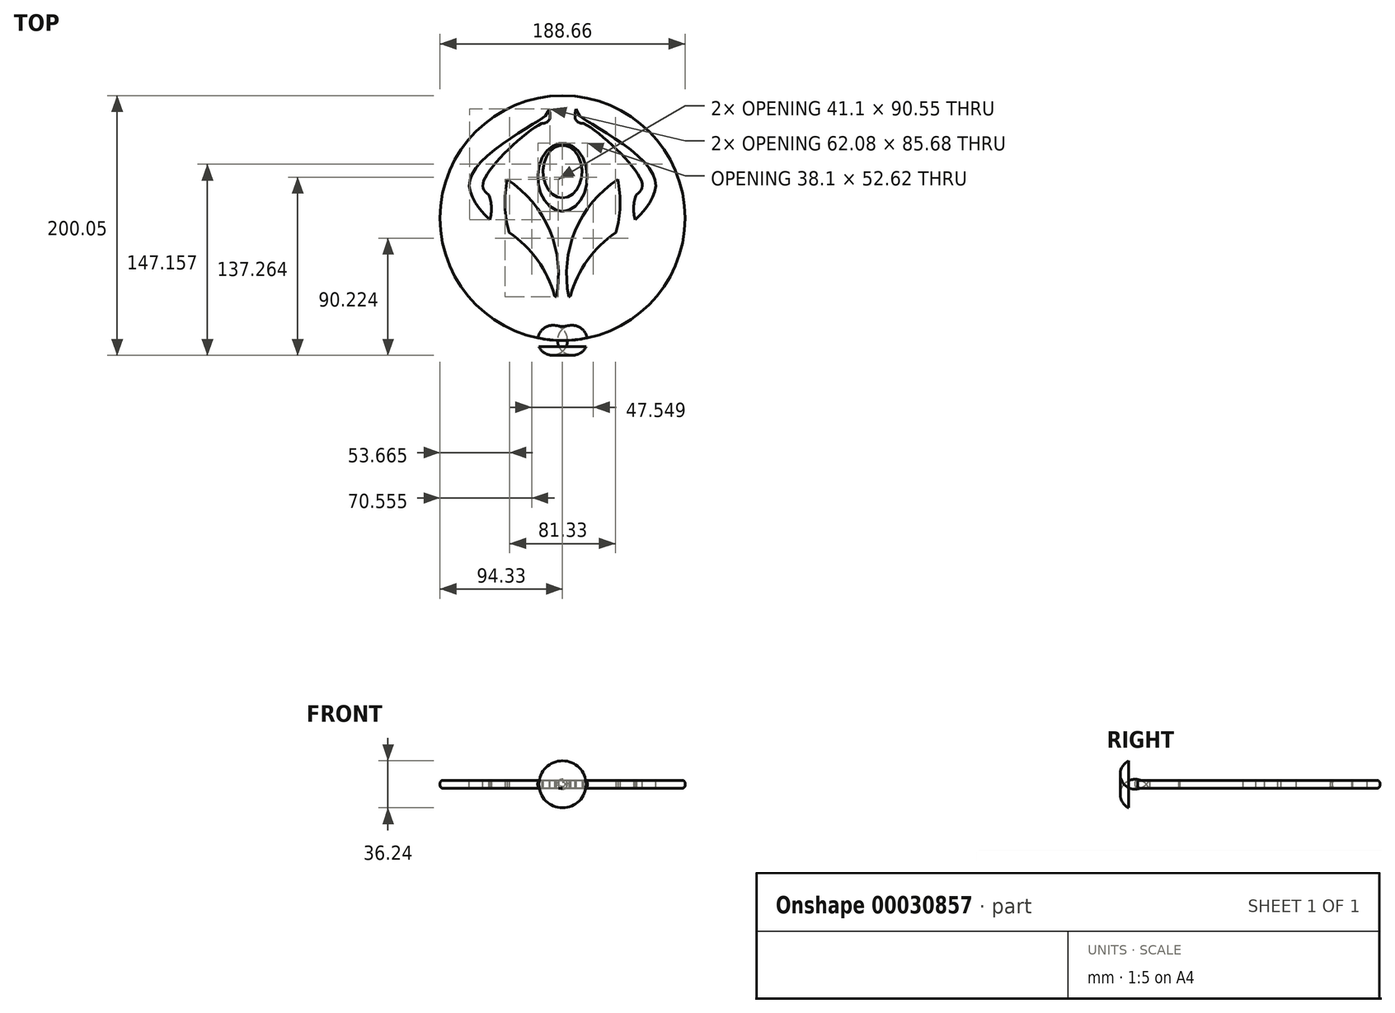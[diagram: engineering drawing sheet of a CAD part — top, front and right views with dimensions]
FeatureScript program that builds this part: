
annotation { "Feature Type Name" : "Feature", "Feature Type Description" : "" }
export const myFeature = defineFeature(function(context is Context, id is Id, definition is map)
    precondition{}
    {
        {
            var Q0;
            Q0=qCreatedBy(makeId("Top.planeOp"),FACE);
            var sketch = newSketch(context, id + "F0", { "sketchPlane" : qUnion([Q0])});
            skLineSegment(sketch, "E0", {"start": v(-75.5, -12.71) * mm, "end": v(-9.56, -74.3) * mm, "construction": true});
            skLineSegment(sketch, "E1", {"start": v(-4.86, -71.61) * mm, "end": v(-42.6, 18.94) * mm, "construction": true});
            skArc(sketch, "E2", {"start": v(-75.5, -12.71) * mm, "mid": v(-51.74, -53.37) * mm, "end": v(-9.56, -74.3) * mm});
            skArc(sketch, "E3", {"start": v(-4.86, -71.61) * mm, "mid": v(-9.83, -20.55) * mm, "end": v(-42.6, 18.94) * mm});
            skArc(sketch, "E4.MirrorCS", {"start": v(-75.5, -12.71) * mm, "mid": v(-33.32, -33.65) * mm, "end": v(-9.56, -74.3) * mm});
            skArc(sketch, "E5.0", {"start": v(-41.12, -22.06) * mm, "mid": v(-19.25, -43.28) * mm, "end": v(-6.12, -70.78) * mm});
            skArc(sketch, "E6.MirrorCS", {"start": v(-4.86, -71.61) * mm, "mid": v(-5.5, -71.2) * mm, "end": v(-6.12, -70.78) * mm});
            skArc(sketch, "E7.trimOffspring", {"start": v(-41.12, -22.06) * mm, "mid": v(-44.3, -1.65) * mm, "end": v(-42.6, 18.94) * mm});
            skArc(sketch, "E8.MirrorCS", {"start": v(75.5, -12.71) * mm, "mid": v(51.74, -53.37) * mm, "end": v(9.56, -74.3) * mm});
            skArc(sketch, "E9.MirrorCS", {"start": v(75.5, -12.71) * mm, "mid": v(33.32, -33.65) * mm, "end": v(9.56, -74.3) * mm});
            skArc(sketch, "E10.MirrorCS", {"start": v(41.12, -22.06) * mm, "mid": v(44.3, -1.65) * mm, "end": v(42.6, 18.94) * mm});
            skArc(sketch, "E11.MirrorCS", {"start": v(41.12, -22.06) * mm, "mid": v(19.25, -43.28) * mm, "end": v(6.12, -70.78) * mm});
            skArc(sketch, "E12.MirrorCS", {"start": v(4.86, -71.61) * mm, "mid": v(9.83, -20.55) * mm, "end": v(42.6, 18.94) * mm});
            skArc(sketch, "E13.MirrorCS", {"start": v(4.86, -71.61) * mm, "mid": v(5.5, -71.2) * mm, "end": v(6.12, -70.78) * mm});
            skFitSpline(sketch, "E14", {"points": [v(-10.08, 72.14) * mm, v(-14.37, 65.7) * mm, v(-68.94, 22.84) * mm, v(-55.76, -13.54) * mm], "startDerivative": vector(-33.58, -68.78) * mm, "endDerivative": vector(100.58, -102.34) * mm});
            skArc(sketch, "E15", {"start": v(-55.76, -13.54) * mm, "mid": v(-54.5, -3.73) * mm, "end": v(-56.62, 5.94) * mm});
            skFitSpline(sketch, "E16", {"points": [v(-56.62, 5.94) * mm, v(-60.66, 15.94) * mm, v(-15.88, 60.9) * mm], "startDerivative": vector(-32.39, 22.42) * mm, "endDerivative": vector(56.1, 28.88) * mm});
            skFitSpline(sketch, "E17", {"points": [v(-10.08, 72.14) * mm, v(-10.08, 63.33) * mm, v(-15.88, 60.9) * mm], "startDerivative": vector(3.32, -19.88) * mm, "endDerivative": vector(-13.95, 1.21) * mm});
            skFitSpline(sketch, "E18.MirrorCS", {"points": [v(10.57, 72.14) * mm, v(10.57, 63.33) * mm, v(16.38, 60.9) * mm], "startDerivative": vector(-3.32, -19.88) * mm, "endDerivative": vector(13.95, 1.21) * mm});
            skFitSpline(sketch, "E19.MirrorCS", {"points": [v(10.57, 72.14) * mm, v(14.86, 65.7) * mm, v(69.43, 22.84) * mm, v(56.26, -13.54) * mm], "startDerivative": vector(33.58, -68.78) * mm, "endDerivative": vector(-100.58, -102.34) * mm});
            skFitSpline(sketch, "E20.MirrorCS", {"points": [v(57.12, 5.94) * mm, v(61.15, 15.94) * mm, v(16.38, 60.9) * mm], "startDerivative": vector(32.39, 22.42) * mm, "endDerivative": vector(-56.1, 28.88) * mm});
            skArc(sketch, "E21.MirrorCS", {"start": v(56.26, -13.54) * mm, "mid": v(55, -3.73) * mm, "end": v(57.12, 5.94) * mm});
            skEllipse(sketch, "E22", {"center": v(0, 20.14) * mm, "majorRadius": 26.3 * mm, "minorRadius": 19.05 * mm, "majorAxis": v(0, -1)});
            skEllipse(sketch, "E23", {"center": v(0, 24.44) * mm, "majorRadius": 20.32 * mm, "minorRadius": 15 * mm, "majorAxis": v(0, -1)});
            skSolve(sketch);
        }
        {
            var Q0;
            Q0=qCreatedBy(makeId("Top.planeOp"),FACE);
            var sketch = newSketch(context, id + "F1", { "sketchPlane" : qUnion([Q0])});
            skEllipse(sketch, "E24", {"center": v(0, 20.7) * mm, "majorRadius": 26.3 * mm, "minorRadius": 19.05 * mm, "majorAxis": v(0, -1)});
            skEllipse(sketch, "E25", {"center": v(0, 25) * mm, "majorRadius": 20.32 * mm, "minorRadius": 15 * mm, "majorAxis": v(0, -1)});
            skSolve(sketch);
        }
        {
            var Q0;
            Q0=qCreatedBy(makeId("Top.planeOp"),FACE);
            var sketch = newSketch(context, id + "F2", { "sketchPlane" : qUnion([Q0])});
            skFitSpline(sketch, "E26", {"points": [v(-10.32, 73.44) * mm, v(-14.62, 66.99) * mm, v(-69.19, 24.14) * mm, v(-56, -12.24) * mm], "startDerivative": vector(-33.58, -68.78) * mm, "endDerivative": vector(100.58, -102.34) * mm});
            skArc(sketch, "E27", {"start": v(-56, -12.24) * mm, "mid": v(-54.75, -2.43) * mm, "end": v(-56.87, 7.24) * mm});
            skFitSpline(sketch, "E28", {"points": [v(-56.87, 7.24) * mm, v(-60.9, 17.24) * mm, v(-16.13, 62.2) * mm], "startDerivative": vector(-32.39, 22.42) * mm, "endDerivative": vector(56.1, 28.88) * mm});
            skFitSpline(sketch, "E29", {"points": [v(-10.32, 73.44) * mm, v(-10.32, 64.63) * mm, v(-16.13, 62.2) * mm], "startDerivative": vector(3.32, -19.88) * mm, "endDerivative": vector(-13.95, 1.21) * mm});
            skFitSpline(sketch, "E30.MirrorCS", {"points": [v(10.32, 73.44) * mm, v(10.32, 64.63) * mm, v(16.13, 62.2) * mm], "startDerivative": vector(-3.32, -19.88) * mm, "endDerivative": vector(13.95, 1.21) * mm});
            skFitSpline(sketch, "E31.MirrorCS", {"points": [v(10.32, 73.44) * mm, v(14.62, 66.99) * mm, v(69.19, 24.14) * mm, v(56, -12.24) * mm], "startDerivative": vector(33.58, -68.78) * mm, "endDerivative": vector(-100.58, -102.34) * mm});
            skFitSpline(sketch, "E32.MirrorCS", {"points": [v(56.87, 7.24) * mm, v(60.9, 17.24) * mm, v(16.13, 62.2) * mm], "startDerivative": vector(32.39, 22.42) * mm, "endDerivative": vector(-56.1, 28.88) * mm});
            skArc(sketch, "E33.MirrorCS", {"start": v(56, -12.24) * mm, "mid": v(54.75, -2.43) * mm, "end": v(56.87, 7.24) * mm});
            skSolve(sketch);
        }
        {
            var Q0;
            Q0=qCreatedBy(makeId("Top.planeOp"),FACE);
            var sketch = newSketch(context, id + "F3", { "sketchPlane" : qUnion([Q0])});
            skCircle(sketch, "E34", {"center": v(0, -10.83) * mm, "radius": 94.33 * mm});
            skSolve(sketch);
        }
        {
            var Q0;
            Q0=makeQuery(id+"F3.imprint","IMPRINT",FACE,{"disambiguationData":[TD([[makeQuery(id+"F3.imprint","IMPRINT",EDGE,{"derivedFrom":sQuery(id+"F3.wireOp",EDGE,"E34")}),1.0]])]});
            extrude(context, id + "F4", {"entities" : qUnion([Q0]), "endBound" : BoundingType.SYMMETRIC, "depth" : 6 * mm});
        }
        {
            var Q0;
            Q0=makeQuery(id+"F0.imprint","IMPRINT",FACE,{"disambiguationData":[TD([[makeQuery(id+"F0.imprint","IMPRINT",EDGE,{"derivedFrom":sQuery(id+"F0.wireOp",EDGE,"E8.MirrorCS")}),-1.0]])]});
            var Q1;
            Q1=makeQuery(id+"F0.imprint","IMPRINT",FACE,{"disambiguationData":[TD([[makeQuery(id+"F0.imprint","IMPRINT",EDGE,{"derivedFrom":sQuery(id+"F0.wireOp",EDGE,"E10.MirrorCS")}),1.0]])]});
            var Q2;
            Q2=makeQuery(id+"F0.imprint","IMPRINT",FACE,{"disambiguationData":[TD([[makeQuery(id+"F0.imprint","IMPRINT",EDGE,{"derivedFrom":sQuery(id+"F0.wireOp",EDGE,"E3")}),1.0]])]});
            var Q3;
            Q3=makeQuery(id+"F0.imprint","IMPRINT",FACE,{"disambiguationData":[TD([[makeQuery(id+"F0.imprint","IMPRINT",EDGE,{"derivedFrom":sQuery(id+"F0.wireOp",EDGE,"E4.MirrorCS")}),-1.0]])]});
            var Q4;
            Q4=makeQuery(id+"F2.imprint","IMPRINT",FACE,{"disambiguationData":[TD([[makeQuery(id+"F2.imprint","IMPRINT",EDGE,{"derivedFrom":sQuery(id+"F2.wireOp",EDGE,"E26")}),1.0]])]});
            var Q5;
            Q5=makeQuery(id+"F2.imprint","IMPRINT",FACE,{"disambiguationData":[TD([[makeQuery(id+"F2.imprint","IMPRINT",EDGE,{"derivedFrom":sQuery(id+"F2.wireOp",EDGE,"E30.MirrorCS")}),1.0]])]});
            var Q6;
            Q6=makeQuery(id+"F1.imprint","IMPRINT",FACE,{"disambiguationData":[TD([[makeQuery(id+"F1.imprint","IMPRINT",EDGE,{"derivedFrom":sQuery(id+"F1.wireOp",EDGE,"E24")}),1.0]])]});
            extrude(context, id + "F5", {"entities" : qUnion([Q0, Q1, Q2, Q3, Q4, Q5, Q6]), "operationType" : NewBodyOperationType.REMOVE, "endBound" : BoundingType.SYMMETRIC, "depth" : 25 * mm});
        }
        {
            var Q0;
            Q0=qCreatedBy(makeId("Front.planeOp"),FACE);
            cPlane(context, id + "F6", {"entities" : qUnion([Q0]), "cplaneType" : CPlaneType.OFFSET, "offset" : 50 * mm, "oppositeDirection" : true, "width" : 150 * mm, "height" : 150 * mm});
        }
        {
            var Q0;
            Q0=qCreatedBy(id+"F6.planeOp",FACE);
            var sketch = newSketch(context, id + "F7", { "sketchPlane" : qUnion([Q0])});
            skCircle(sketch, "E35", {"center": v(0, 0) * mm, "radius": 1.81 * mm});
            skSolve(sketch);
        }
        {
            var Q0;
            Q0 = qSketchRegion(id + "F7", true);
            var Q1;
            Q1=makeQuery(id+"F5.boolean.opBoolean","COPY",FACE,{"derivedFrom":makeQuery(id+"F5.opExtrude","SWEPT_FACE",FACE,{"disambiguationData":[OSD([sQuery(id+"F1.wireOp",EDGE,"E25")])]})});
            extrude(context, id + "F8", {"entities" : qUnion([Q0]), "operationType" : NewBodyOperationType.ADD, "endBound" : BoundingType.UP_TO_SURFACE, "endBoundEntityFace" : qUnion([Q1]), "depth" : 25 * mm});
        }
        {
            var Q0;
            Q0=makeQuery(id+"F4.opExtrude","CAP_EDGE",EDGE,{"disambiguationData":[OSD([sQuery(id+"F3.wireOp",EDGE,"E34")])],"isStart":false});
            var Q1;
            Q1=makeQuery(id+"F4.opExtrude","CAP_EDGE",EDGE,{"disambiguationData":[OSD([sQuery(id+"F3.wireOp",EDGE,"E34")])],"isStart":true});
            fillet(context, id + "F9", {"entities" : qUnion([Q0, Q1]), "radius" : 2 * mm, "tangentPropagation" : true, "allowEdgeOverflow" : false});
        }
        {
            var Q0;
            Q0=qCreatedBy(makeId("Right.planeOp"),FACE);
            var sketch = newSketch(context, id + "F10", { "sketchPlane" : qUnion([Q0])});
            skLineSegment(sketch, "E36", {"start": v(0, 0) * mm, "end": v(-123.4, 0) * mm, "construction": true});
            skLineSegment(sketch, "E37", {"start": v(-109.98, 18.12) * mm, "end": v(-109.98, 0) * mm});
            skLineSegment(sketch, "E38", {"start": v(-109.98, 0) * mm, "end": v(-96.4, 0) * mm});
            skArc(sketch, "E39", {"start": v(-96.4, 0) * mm, "mid": v(-95.77, 14.62) * mm, "end": v(-109.98, 18.12) * mm});
            skSolve(sketch);
        }
        {
            var Q0;
            Q0=makeQuery(id+"F10.imprint","IMPRINT",FACE,{"disambiguationData":[TD([[makeQuery(id+"F10.imprint","IMPRINT",EDGE,{"derivedFrom":sQuery(id+"F10.wireOp",EDGE,"E37")}),1.0]])]});
            var Q1;
            Q1=sQuery(id+"F10.wireOp",EDGE,"E36");
            revolve(context, id + "F11", {"entities" : qUnion([Q0]), "axis" : qUnion([Q1]), "revolveType" : RevolveType.FULL});
        }
        {
            var Q0;
            Q0=makeQuery(id+"F5.boolean.opBoolean","SPLIT",BODY,{"disambiguationData":[OD(0.0)],"derivedFrom":makeQuery(id+"F4.opExtrude","SWEPT_BODY",BODY,{"disambiguationData":[OSD([sQuery(id+"F3.wireOp",EDGE,"E34")])]})});
            var Q1;
            Q1=makeQuery(id+"F11.opRevolve","SWEPT_BODY",BODY,{"disambiguationData":[OSD([sQuery(id+"F10.wireOp",EDGE,"E37"),sQuery(id+"F10.wireOp",EDGE,"E38"),sQuery(id+"F10.wireOp",EDGE,"E39")])]});
            booleanBodies(context, id + "F12", {"operationType" : BooleanOperationType.SUBTRACTION, "tools" : qUnion([Q0]), "targets" : qUnion([Q1]), "keepTools" : true});
        }
    });
